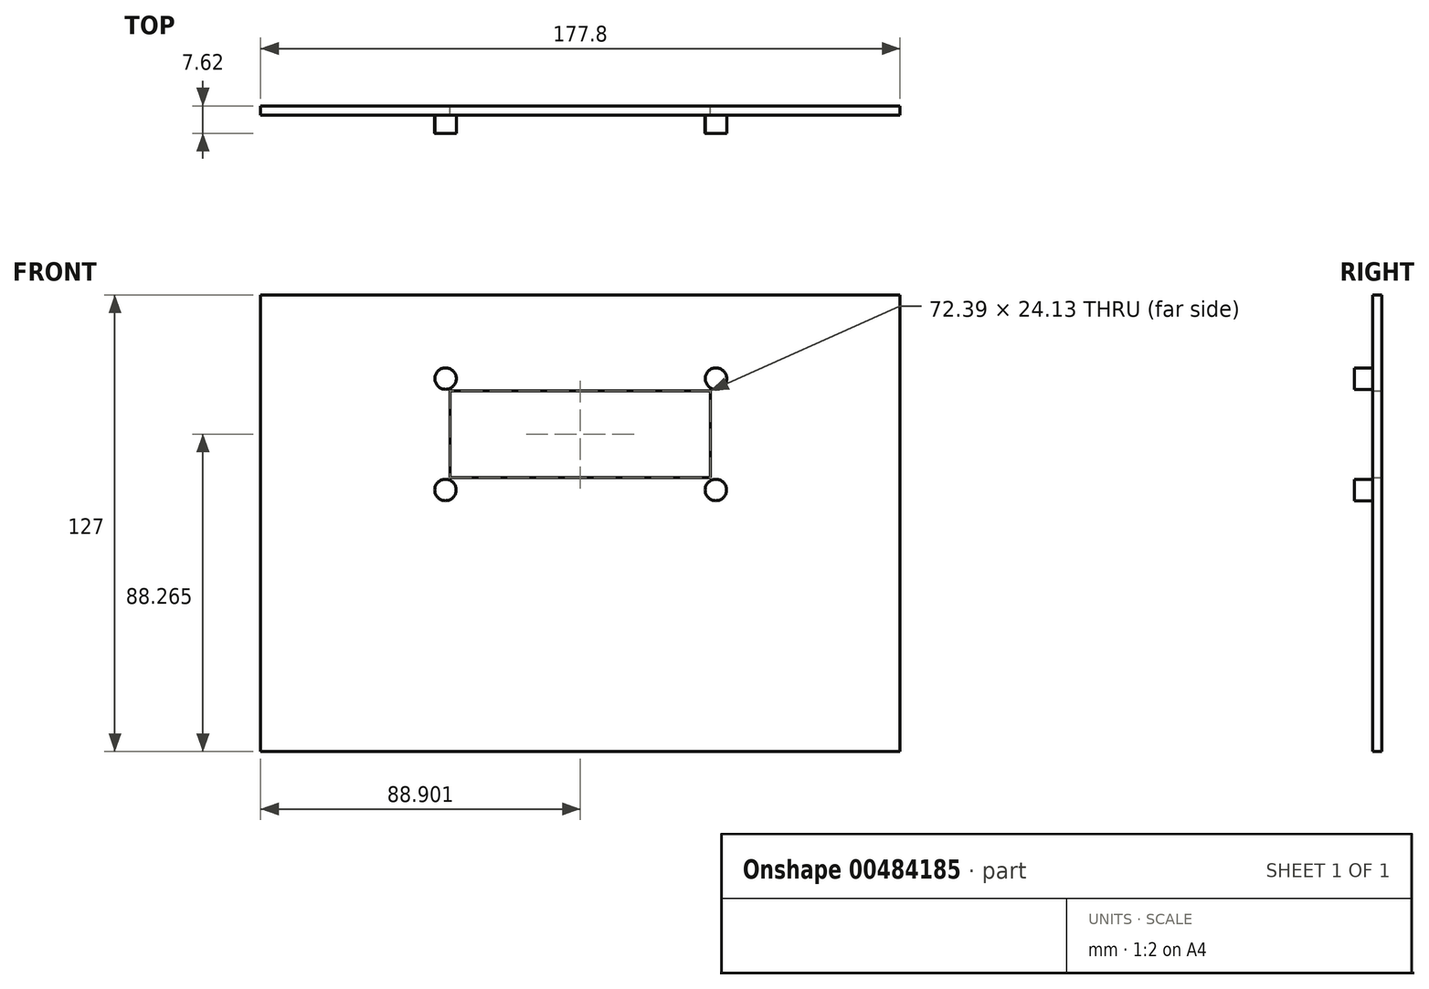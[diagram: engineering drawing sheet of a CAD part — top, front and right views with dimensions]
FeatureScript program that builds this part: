
annotation { "Feature Type Name" : "Feature", "Feature Type Description" : "" }
export const myFeature = defineFeature(function(context is Context, id is Id, definition is map)
    precondition{}
    {
        {
            var Q0;
            Q0=qCreatedBy(makeId("Front.planeOp"),FACE);
            var sketch = newSketch(context, id + "F0", { "sketchPlane" : qUnion([Q0])});
            skLineSegment(sketch, "E0.bottom", {"start": v(-89.14, 63.5) * mm, "end": v(88.66, 63.5) * mm});
            skLineSegment(sketch, "E0.top", {"start": v(-89.14, -63.5) * mm, "end": v(88.66, -63.5) * mm});
            skLineSegment(sketch, "E0.left", {"start": v(-89.14, 63.5) * mm, "end": v(-89.14, -63.5) * mm});
            skLineSegment(sketch, "E0.right", {"start": v(88.66, 63.5) * mm, "end": v(88.66, -63.5) * mm});
            skLineSegment(sketch, "E1.bottom", {"start": v(-36.43, 36.83) * mm, "end": v(35.96, 36.83) * mm});
            skLineSegment(sketch, "E1.top", {"start": v(-36.43, 12.7) * mm, "end": v(35.96, 12.7) * mm});
            skLineSegment(sketch, "E1.left", {"start": v(-36.43, 36.83) * mm, "end": v(-36.43, 12.7) * mm});
            skLineSegment(sketch, "E1.right", {"start": v(35.96, 36.83) * mm, "end": v(35.96, 12.7) * mm});
            skLineSegment(sketch, "E2", {"start": v(-0.24, -63.5) * mm, "end": v(-0.24, -63.5) * mm});
            skPoint(sketch, "E2.startSnap0", {"position": v(-0.24, 12.7) * mm});
            skCircle(sketch, "E3", {"center": v(37.44, 9.27) * mm, "radius": 2.98 * mm});
            skCircle(sketch, "E4", {"center": v(-37.74, 9.27) * mm, "radius": 2.98 * mm});
            skCircle(sketch, "E5", {"center": v(37.48, 40.26) * mm, "radius": 2.98 * mm});
            skCircle(sketch, "E6", {"center": v(-37.7, 40.26) * mm, "radius": 2.98 * mm});
            skSolve(sketch);
        }
        {
            var Q0;
            Q0 = qSketchRegion(id + "F0", true);
            extrude(context, id + "F1", {"entities" : qUnion([Q0]), "depth" : 2.54 * mm, "offsetDistance" : 25.4 * mm});
        }
        {
            var Q0;
            Q0=makeQuery(id+"F0.imprint","IMPRINT",FACE,{"disambiguationData":[TD([[makeQuery(id+"F0.imprint","IMPRINT",EDGE,{"derivedFrom":sQuery(id+"F0.wireOp",EDGE,"E6")}),1.0]])]});
            var Q1;
            Q1=makeQuery(id+"F0.imprint","IMPRINT",FACE,{"disambiguationData":[TD([[makeQuery(id+"F0.imprint","IMPRINT",EDGE,{"derivedFrom":sQuery(id+"F0.wireOp",EDGE,"E5")}),1.0]])]});
            var Q2;
            Q2=makeQuery(id+"F0.imprint","IMPRINT",FACE,{"disambiguationData":[TD([[makeQuery(id+"F0.imprint","IMPRINT",EDGE,{"derivedFrom":sQuery(id+"F0.wireOp",EDGE,"E3")}),1.0]])]});
            var Q3;
            Q3=makeQuery(id+"F0.imprint","IMPRINT",FACE,{"disambiguationData":[TD([[makeQuery(id+"F0.imprint","IMPRINT",EDGE,{"derivedFrom":sQuery(id+"F0.wireOp",EDGE,"E4")}),1.0]])]});
            var Q4;
            Q4=makeQuery(id+"F1.opExtrude","SWEPT_BODY",BODY,{"disambiguationData":[OSD([sQuery(id+"F0.wireOp",EDGE,"E0.bottom"),sQuery(id+"F0.wireOp",EDGE,"E0.top"),sQuery(id+"F0.wireOp",EDGE,"E0.left"),sQuery(id+"F0.wireOp",EDGE,"E0.right"),sQuery(id+"F0.wireOp",EDGE,"E1.bottom"),sQuery(id+"F0.wireOp",EDGE,"E1.top"),sQuery(id+"F0.wireOp",EDGE,"E1.left"),sQuery(id+"F0.wireOp",EDGE,"E1.right"),sQuery(id+"F0.wireOp",EDGE,"E3"),sQuery(id+"F0.wireOp",EDGE,"E4"),sQuery(id+"F0.wireOp",EDGE,"E5"),sQuery(id+"F0.wireOp",EDGE,"E6")])]});
            extrude(context, id + "F2", {"entities" : qUnion([Q0, Q1, Q2, Q3]), "operationType" : NewBodyOperationType.ADD, "depth" : 7.62 * mm, "endBoundEntityBody" : qUnion([Q4]), "offsetDistance" : 25.4 * mm});
        }
    });
